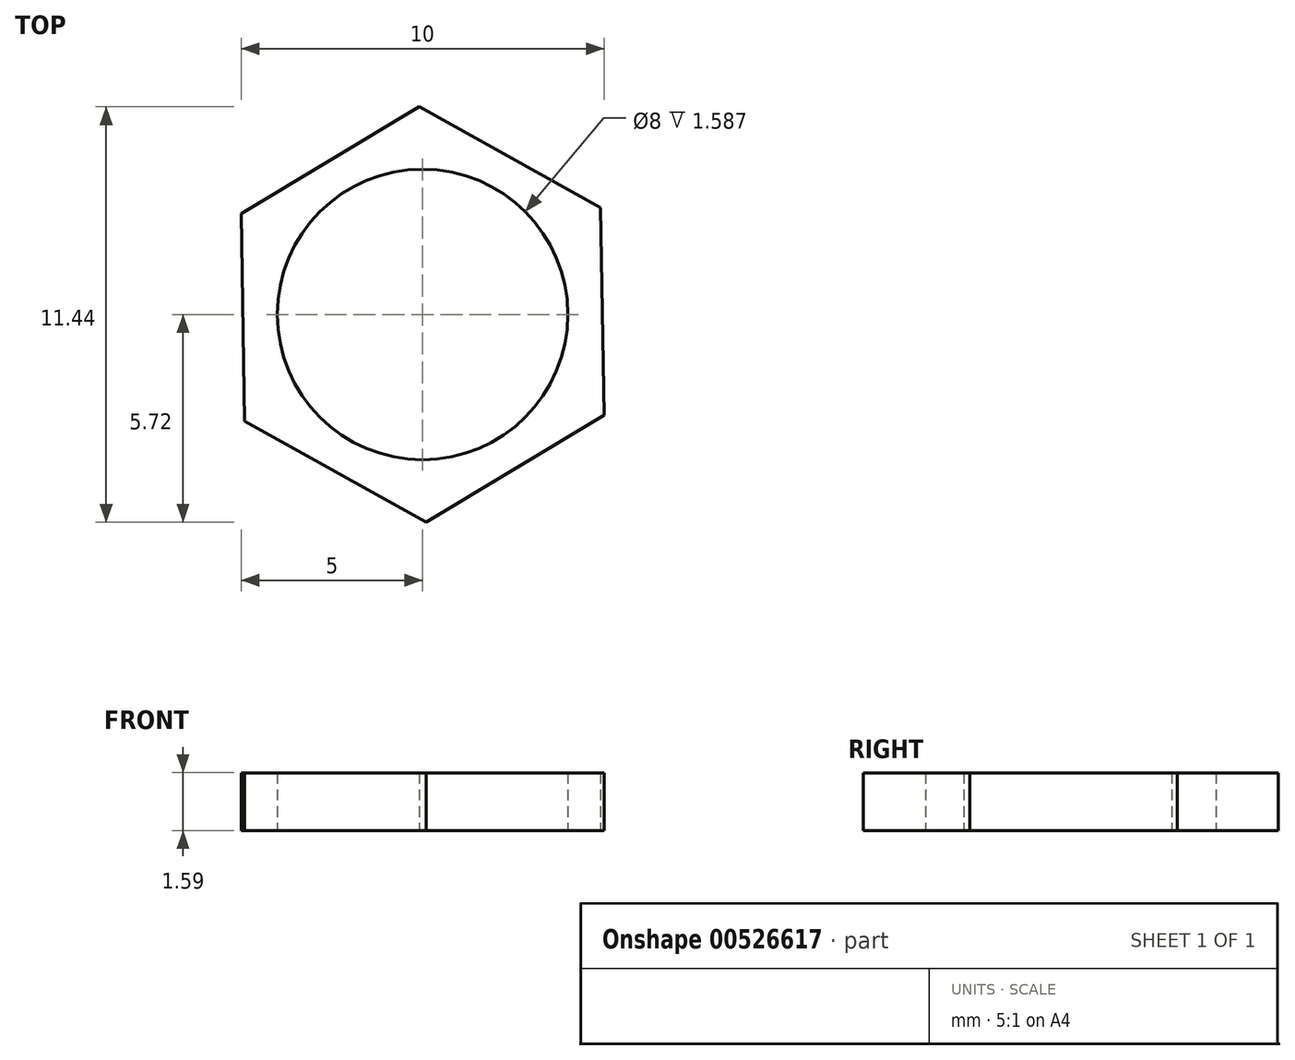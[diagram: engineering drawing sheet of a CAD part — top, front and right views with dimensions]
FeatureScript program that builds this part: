
annotation { "Feature Type Name" : "Feature", "Feature Type Description" : "" }
export const myFeature = defineFeature(function(context is Context, id is Id, definition is map)
    precondition{}
    {
        {
            var Q0;
            Q0=qCreatedBy(makeId("Top.planeOp"),FACE);
            var sketch = newSketch(context, id + "F0", { "sketchPlane" : qUnion([Q0])});
            skCircle(sketch, "E0.cCircle", {"center": v(0, 0) * mm, "radius": 4.95 * mm, "construction": true});
            skLineSegment(sketch, "E0.0", {"start": v(-5, 2.78) * mm, "end": v(-0.1, 5.72) * mm});
            skLineSegment(sketch, "E0.1", {"start": v(-0.1, 5.72) * mm, "end": v(4.9, 2.94) * mm});
            skLineSegment(sketch, "E0.2", {"start": v(4.9, 2.94) * mm, "end": v(5, -2.78) * mm});
            skLineSegment(sketch, "E0.3", {"start": v(5, -2.78) * mm, "end": v(0.1, -5.72) * mm});
            skLineSegment(sketch, "E0.4", {"start": v(0.1, -5.72) * mm, "end": v(-4.9, -2.94) * mm});
            skLineSegment(sketch, "E0.5", {"start": v(-4.9, -2.94) * mm, "end": v(-5, 2.78) * mm});
            skPoint(sketch, "E0.0.midPoint", {"position": v(-2.55, 4.25) * mm});
            skCircle(sketch, "E1", {"center": v(0, 0) * mm, "radius": 4 * mm});
            skSolve(sketch);
        }
        {
            var Q0;
            Q0 = qSketchRegion(id + "F0", true);
            extrude(context, id + "F1", {"entities" : qUnion([Q0]), "depth" : 1.59 * mm, "offsetDistance" : 25.4 * mm});
        }
    });
